# Revit family: _FHF-EA_EM
name_source: partatom
category: Pipe Accessories
units: mm (PartAtom-declared; Revit-internal decimal feet)

## family parameters
Always vertical = Yes
Cut with Voids When Loaded = No
OmniClass Number = 23.65.55.14.17
OmniClass Title = Adjusting/Controlling Valves for Liquid Services
Part Type = Normal
Round Connector Dimension = Use Diameter
Shared = Yes
Work Plane-Based = No

## types (2) — shared parameters
Description = Accessories for Manifolds
H = 129 mm
H1 = 76 mm
H2 = 54 mm
IfcExportAs = IfcValveType
L = 80 mm
Manufacturer = Danfoss
Valve Body Material = Danfoss Brass
W = 36 mm  [stored 0.11811 ft]

## per-type parameters (varying)
| type | FHF-EA | FHF-EM | IfcExportType | Model | Model Type |
| FHF-EM_088U0786 | No | Yes | FHF-EM | 088U0786 | FHF-EM_End section with manual airvent |
| FHF-EA_088U0785 | Yes | No | FHF-EA | 088U0785 | FHF-EA_End section with automatic airvent |

note: [stored X ft] marks values corroborated as IEEE doubles in the binary element streams (Revit-internal decimal feet)

## geometry (parser evidence)
native form markers: Blend x2, Sweep x3
no freeform markers — native parametric forms only
